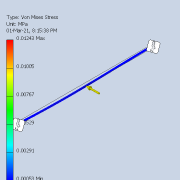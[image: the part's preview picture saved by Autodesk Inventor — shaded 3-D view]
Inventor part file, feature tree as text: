
AUTODESK INVENTOR PART (.ipt)
format: ipt  version: 2020 (Build 240168000, 168)  size: 116,224 bytes
history: native  units: mm
features: extrude x1, sketch x1
ambient origin geometry x8: Origin, YZ Plane, XZ Plane, XY Plane, X Axis, Y Axis, Z Axis, Center Point
bodies: Solid1 (feature_tree)
feature tree (2):
  extrude  "Extrusion1"  Depth=570.0mm TaperAngle=0.0deg
  sketch  "Sketch1"  dims[d0=10.0mm d1=570.0mm d2=0.0mm]
